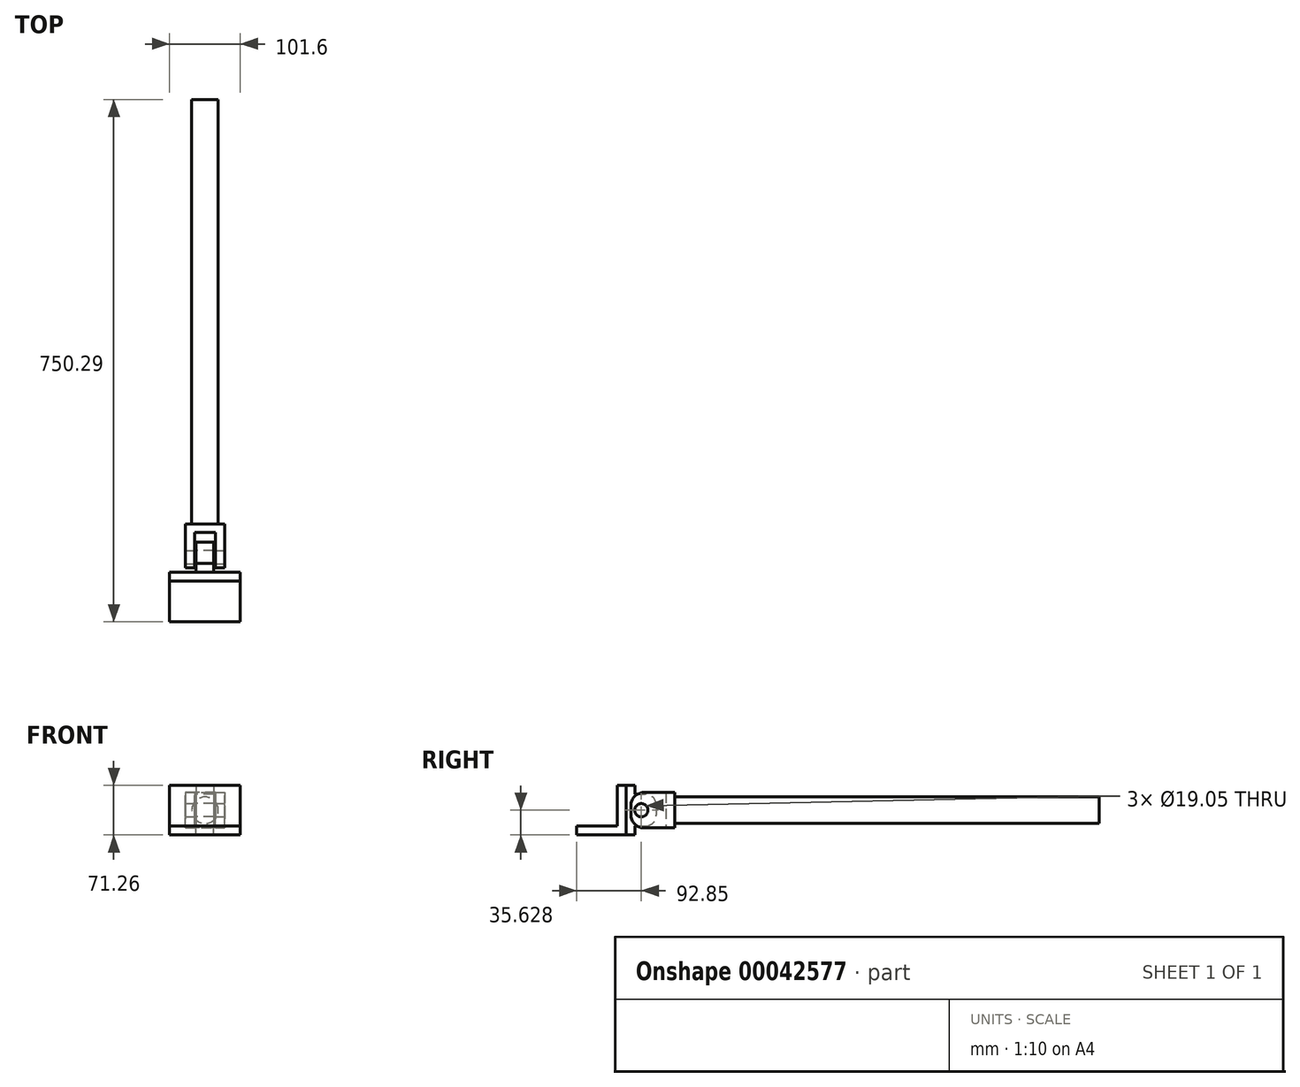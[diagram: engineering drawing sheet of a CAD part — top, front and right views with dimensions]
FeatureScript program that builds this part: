
annotation { "Feature Type Name" : "Feature", "Feature Type Description" : "" }
export const myFeature = defineFeature(function(context is Context, id is Id, definition is map)
    precondition{}
    {
        {
            var Q0;
            Q0=qCreatedBy(makeId("Right.planeOp"),FACE);
            var sketch = newSketch(context, id + "F0", { "sketchPlane" : qUnion([Q0])});
            skLineSegment(sketch, "E0", {"start": v(0, 0) * mm, "end": v(0, 71.26) * mm});
            skLineSegment(sketch, "E1", {"start": v(0, 71.26) * mm, "end": v(-12.7, 71.26) * mm});
            skLineSegment(sketch, "E2", {"start": v(-12.7, 71.26) * mm, "end": v(-12.7, 12.7) * mm});
            skLineSegment(sketch, "E3", {"start": v(-12.7, 12.7) * mm, "end": v(-71.26, 12.7) * mm});
            skLineSegment(sketch, "E4", {"start": v(-71.26, 12.7) * mm, "end": v(-71.26, 0) * mm});
            skLineSegment(sketch, "E5", {"start": v(-71.26, 0) * mm, "end": v(0, 0) * mm});
            skSolve(sketch);
        }
        {
            var Q0;
            Q0=makeQuery(id+"F0.imprint","IMPRINT",FACE,{"disambiguationData":[TD([[makeQuery(id+"F0.imprint","IMPRINT",EDGE,{"derivedFrom":sQuery(id+"F0.wireOp",EDGE,"E0")}),1.0]])]});
            extrude(context, id + "F1", {"entities" : qUnion([Q0]), "endBound" : BoundingType.SYMMETRIC, "depth" : 101.6 * mm});
        }
        {
            var Q0;
            Q0=makeQuery(id+"F1.opExtrude","SWEPT_FACE",FACE,{"disambiguationData":[OSD([sQuery(id+"F0.wireOp",EDGE,"E0")])]});
            var sketch = newSketch(context, id + "F2", { "sketchPlane" : qUnion([Q0])});
            skLineSegment(sketch, "E6.rect.bottom", {"start": v(-12.7, 71.26) * mm, "end": v(12.7, 71.26) * mm});
            skLineSegment(sketch, "E6.rect.top", {"start": v(-12.7, 0) * mm, "end": v(12.7, 0) * mm});
            skLineSegment(sketch, "E6.rect.left", {"start": v(-12.7, 71.26) * mm, "end": v(-12.7, 0) * mm});
            skLineSegment(sketch, "E6.rect.right", {"start": v(12.7, 71.26) * mm, "end": v(12.7, 0) * mm});
            skPoint(sketch, "E6.rect.middle", {"position": v(0, 35.63) * mm});
            skLineSegment(sketch, "E7", {"start": v(0, 0) * mm, "end": v(0, 35.63) * mm, "construction": true});
            skSolve(sketch);
        }
        {
            var Q0;
            Q0=makeQuery(id+"F2.imprint","IMPRINT",FACE,{"disambiguationData":[TD([[makeQuery(id+"F2.imprint","IMPRINT",EDGE,{"derivedFrom":sQuery(id+"F2.wireOp",EDGE,"E6.rect.bottom")}),-1.0]])]});
            var Q1;
            Q1=sQuery(id+"F2.wireOp",EDGE,"E6.rect.left");
            var Q2;
            Q2=sQuery(id+"F2.wireOp",EDGE,"E6.rect.bottom");
            var Q3;
            Q3=sQuery(id+"F2.wireOp",EDGE,"E6.rect.right");
            extrude(context, id + "F3", {"entities" : qUnion([Q0]), "surfaceEntities" : qUnion([Q1, Q2, Q3]), "depth" : 43.18 * mm});
        }
        {
            var Q0;
            Q0=makeQuery(id+"F3.opExtrude","SWEPT_FACE",FACE,{"disambiguationData":[OSD([sQuery(id+"F2.wireOp",EDGE,"E6.rect.right")])]});
            var sketch = newSketch(context, id + "F4", { "sketchPlane" : qUnion([Q0])});
            skCircle(sketch, "E8", {"center": v(-21.59, 35.63) * mm, "radius": 9.53 * mm});
            skLineSegment(sketch, "E9", {"start": v(-43.18, 35.63) * mm, "end": v(0, 35.63) * mm, "construction": true});
            skSolve(sketch);
        }
        {
            var Q0;
            Q0=makeQuery(id+"F4.imprint","IMPRINT",FACE,{"disambiguationData":[TD([[makeQuery(id+"F4.imprint","IMPRINT",EDGE,{"derivedFrom":sQuery(id+"F4.wireOp",EDGE,"E8")}),1.0]])]});
            extrude(context, id + "F5", {"entities" : qUnion([Q0]), "operationType" : NewBodyOperationType.REMOVE, "endBound" : BoundingType.THROUGH_ALL, "oppositeDirection" : true, "depth" : 25.4 * mm});
        }
        {
            var Q0;
            Q0=makeQuery(id+"F3.opExtrude","SWEPT_FACE",FACE,{"disambiguationData":[OSD([sQuery(id+"F2.wireOp",EDGE,"E6.rect.right")])]});
            var sketch = newSketch(context, id + "F6", { "sketchPlane" : qUnion([Q0])});
            skLineSegment(sketch, "E10", {"start": v(0, 71.26) * mm, "end": v(-12.7, 71.26) * mm, "construction": true});
            skLineSegment(sketch, "E11", {"start": v(-12.7, 71.26) * mm, "end": v(-12.7, 58.56) * mm});
            skLineSegment(sketch, "E12", {"start": v(-12.7, 58.56) * mm, "end": v(-27.3, 58.56) * mm});
            skLineSegment(sketch, "E13", {"start": v(-43.18, 42.68) * mm, "end": v(-43.18, 35.63) * mm});
            skLineSegment(sketch, "E14", {"start": v(-43.18, 35.63) * mm, "end": v(0, 35.63) * mm, "construction": true});
            skPoint(sketch, "E15.visualSharp", {"position": v(-43.18, 58.56) * mm});
            skArc(sketch, "E15.filletArc", {"start": v(-27.3, 58.56) * mm, "mid": v(-38.53, 53.9) * mm, "end": v(-43.18, 42.68) * mm});
            skLineSegment(sketch, "E16.MirrorCS", {"start": v(0, 0) * mm, "end": v(-12.7, 0) * mm, "construction": true});
            skLineSegment(sketch, "E17.MirrorCS", {"start": v(-12.7, 0) * mm, "end": v(-12.7, 12.7) * mm});
            skLineSegment(sketch, "E18.MirrorCS", {"start": v(-12.7, 12.7) * mm, "end": v(-27.3, 12.7) * mm});
            skArc(sketch, "E19.MirrorCS", {"start": v(-27.3, 12.7) * mm, "mid": v(-38.53, 17.35) * mm, "end": v(-43.18, 28.57) * mm});
            skLineSegment(sketch, "E20.MirrorCS", {"start": v(-43.18, 28.58) * mm, "end": v(-43.18, 35.63) * mm});
            skLineSegment(sketch, "E21", {"start": v(-12.7, 71.26) * mm, "end": v(-43.18, 71.26) * mm});
            skLineSegment(sketch, "E22", {"start": v(-43.18, 71.26) * mm, "end": v(-43.18, 42.68) * mm});
            skLineSegment(sketch, "E23", {"start": v(-12.7, 0) * mm, "end": v(-43.18, 0) * mm});
            skLineSegment(sketch, "E24", {"start": v(-43.18, 0) * mm, "end": v(-43.18, 28.57) * mm});
            skSolve(sketch);
        }
        {
            var Q0;
            Q0 = qSketchRegion(id + "F6", true);
            extrude(context, id + "F7", {"entities" : qUnion([Q0]), "operationType" : NewBodyOperationType.REMOVE, "endBound" : BoundingType.THROUGH_ALL, "oppositeDirection" : true, "depth" : 25.4 * mm});
        }
        {
            var Q0;
            Q0=makeQuery(id+"F7.boolean.opBoolean","COPY",FACE,{"derivedFrom":makeQuery(id+"F7.opExtrude","SWEPT_FACE",FACE,{"disambiguationData":[OSD([sQuery(id+"F6.wireOp",EDGE,"E12")])]})});
            var Q1;
            Q1=makeQuery(id+"F7.boolean.opBoolean","COPY",FACE,{"derivedFrom":makeQuery(id+"F7.opExtrude","SWEPT_FACE",FACE,{"disambiguationData":[OSD([sQuery(id+"F6.wireOp",EDGE,"E18.MirrorCS")])]})});
            cPlane(context, id + "F8", {"entities" : qUnion([Q0, Q1]), "cplaneType" : CPlaneType.MID_PLANE, "offset" : 152.4 * mm, "width" : 152.4 * mm, "height" : 152.4 * mm});
        }
        {
            var Q0;
            Q0=qCreatedBy(id+"F8.planeOp",FACE);
            var sketch = newSketch(context, id + "F9", { "sketchPlane" : qUnion([Q0])});
            skLineSegment(sketch, "E25", {"start": v(15.12, 6.48) * mm, "end": v(28.43, 6.48) * mm});
            skLineSegment(sketch, "E26", {"start": v(28.43, 6.48) * mm, "end": v(28.43, 69.43) * mm});
            skLineSegment(sketch, "E27", {"start": v(15.12, 6.48) * mm, "end": v(15.12, 57.03) * mm});
            skLineSegment(sketch, "E28", {"start": v(0, 83.37) * mm, "end": v(0, 0) * mm, "construction": true});
            skLineSegment(sketch, "E29.MirrorCS", {"start": v(-15.12, 6.48) * mm, "end": v(-15.12, 57.03) * mm});
            skLineSegment(sketch, "E30.MirrorCS", {"start": v(-15.12, 6.48) * mm, "end": v(-28.43, 6.48) * mm});
            skLineSegment(sketch, "E31.MirrorCS", {"start": v(-28.43, 6.48) * mm, "end": v(-28.43, 69.43) * mm});
            skLineSegment(sketch, "E32", {"start": v(15.12, 57.03) * mm, "end": v(-15.12, 57.03) * mm});
            skLineSegment(sketch, "E33", {"start": v(-28.43, 69.43) * mm, "end": v(28.43, 69.43) * mm});
            skSolve(sketch);
        }
        {
            var Q0;
            Q0=makeQuery(id+"F9.imprint","IMPRINT",FACE,{"disambiguationData":[TD([[makeQuery(id+"F9.imprint","IMPRINT",EDGE,{"derivedFrom":sQuery(id+"F9.wireOp",EDGE,"E25")}),1.0]])]});
            extrude(context, id + "F10", {"entities" : qUnion([Q0]), "endBound" : BoundingType.SYMMETRIC, "depth" : 50.8 * mm});
        }
        {
            var Q0;
            Q0=makeQuery(id+"F10.opExtrude","CAP_EDGE",EDGE,{"disambiguationData":[OSD([sQuery(id+"F9.wireOp",EDGE,"E25")])],"isStart":false});
            var Q1;
            Q1=makeQuery(id+"F10.opExtrude","CAP_EDGE",EDGE,{"disambiguationData":[OSD([sQuery(id+"F9.wireOp",EDGE,"E30.MirrorCS")])],"isStart":false});
            var Q2;
            Q2=makeQuery(id+"F10.opExtrude","CAP_EDGE",EDGE,{"disambiguationData":[OSD([sQuery(id+"F9.wireOp",EDGE,"E25")])],"isStart":true});
            var Q3;
            Q3=makeQuery(id+"F10.opExtrude","CAP_EDGE",EDGE,{"disambiguationData":[OSD([sQuery(id+"F9.wireOp",EDGE,"E30.MirrorCS")])],"isStart":true});
            fillet(context, id + "F11", {"entities" : qUnion([Q0, Q1, Q2, Q3]), "radius" : 19.05 * mm, "tangentPropagation" : true, "allowEdgeOverflow" : false});
        }
        {
            var Q0;
            Q0=makeQuery(id+"F10.opExtrude","SWEPT_FACE",FACE,{"disambiguationData":[OSD([sQuery(id+"F9.wireOp",EDGE,"E26")])]});
            var sketch = newSketch(context, id + "F12", { "sketchPlane" : qUnion([Q0])});
            skCircle(sketch, "E34", {"center": v(21.59, 35.63) * mm, "radius": 9.53 * mm});
            skSolve(sketch);
        }
        {
            var Q0;
            Q0=makeQuery(id+"F12.imprint","IMPRINT",FACE,{"disambiguationData":[TD([[makeQuery(id+"F12.imprint","IMPRINT",EDGE,{"derivedFrom":sQuery(id+"F12.wireOp",EDGE,"E34")}),1.0]])]});
            var Q1;
            Q1=sQuery(id+"F12.wireOp",EDGE,"E34");
            extrude(context, id + "F13", {"entities" : qUnion([Q0]), "operationType" : NewBodyOperationType.REMOVE, "surfaceEntities" : qUnion([Q1]), "endBound" : BoundingType.THROUGH_ALL, "oppositeDirection" : true, "depth" : 25.4 * mm});
        }
        {
            var Q0;
            Q0=makeQuery(id+"F10.opExtrude","SWEPT_FACE",FACE,{"disambiguationData":[OSD([sQuery(id+"F9.wireOp",EDGE,"E33")])]});
            var sketch = newSketch(context, id + "F14", { "sketchPlane" : qUnion([Q0])});
            skCircle(sketch, "E35", {"center": v(0, 35.63) * mm, "radius": 19.05 * mm});
            skLineSegment(sketch, "E36", {"start": v(0, 10.23) * mm, "end": v(0, 35.63) * mm, "construction": true});
            skLineSegment(sketch, "E37", {"start": v(-28.43, 35.63) * mm, "end": v(0, 35.63) * mm, "construction": true});
            skSolve(sketch);
        }
        {
            var Q0;
            Q0=makeQuery(id+"F14.imprint","IMPRINT",FACE,{"disambiguationData":[TD([[makeQuery(id+"F14.imprint","IMPRINT",EDGE,{"derivedFrom":sQuery(id+"F14.wireOp",EDGE,"E35")}),1.0]])]});
            extrude(context, id + "F15", {"entities" : qUnion([Q0]), "depth" : 609.6 * mm});
        }
    });
